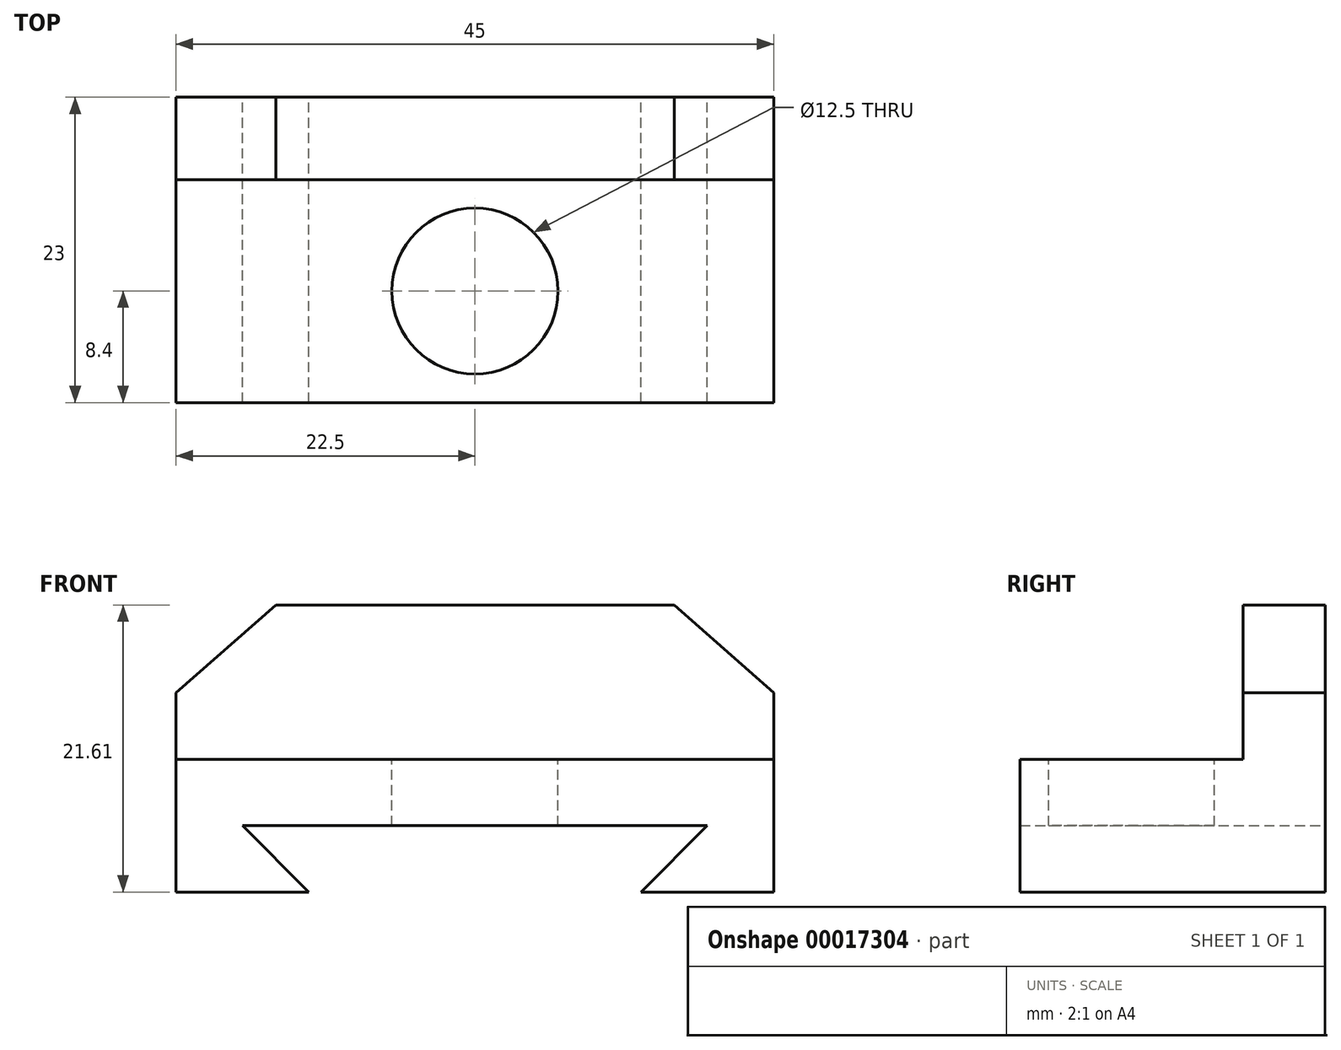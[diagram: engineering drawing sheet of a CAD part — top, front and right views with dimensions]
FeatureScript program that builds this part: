
annotation { "Feature Type Name" : "Feature", "Feature Type Description" : "" }
export const myFeature = defineFeature(function(context is Context, id is Id, definition is map)
    precondition{}
    {
        {
            var Q0;
            Q0=qCreatedBy(makeId("Front.planeOp"),FACE);
            var sketch = newSketch(context, id + "F0", { "sketchPlane" : qUnion([Q0])});
            skLineSegment(sketch, "E0", {"start": v(0, 15) * mm, "end": v(7.5, 21.61) * mm});
            skLineSegment(sketch, "E1", {"start": v(7.5, 21.61) * mm, "end": v(37.5, 21.61) * mm});
            skLineSegment(sketch, "E2", {"start": v(37.5, 21.61) * mm, "end": v(45, 15) * mm});
            skLineSegment(sketch, "E3", {"start": v(45, 15) * mm, "end": v(45, 0) * mm});
            skLineSegment(sketch, "E4", {"start": v(45, 10) * mm, "end": v(0, 10) * mm});
            skLineSegment(sketch, "E5", {"start": v(10, 0) * mm, "end": v(5, 5) * mm});
            skLineSegment(sketch, "E6", {"start": v(5, 5) * mm, "end": v(40, 5) * mm});
            skLineSegment(sketch, "E7", {"start": v(40, 5) * mm, "end": v(35, 0) * mm});
            skLineSegment(sketch, "E8", {"start": v(0, 0) * mm, "end": v(10, 0) * mm});
            skLineSegment(sketch, "E9", {"start": v(35, 0) * mm, "end": v(45, 0) * mm});
            skLineSegment(sketch, "E10", {"start": v(0, 5) * mm, "end": v(0, 0) * mm});
            skLineSegment(sketch, "E11", {"start": v(0, 15) * mm, "end": v(0, 5) * mm});
            skSolve(sketch);
        }
        {
            var Q0;
            {var subQ2=sQuery(id+"F0.wireOp",EDGE,"E4");Q0=makeQuery(id+"F0.imprint","IMPRINT",FACE,{"disambiguationData":[TD([[makeQuery(id+"F0.imprint","IMPRINT",EDGE,{"derivedFrom":subQ2}),1.0]])]});}
            var Q1;
            {var subQ2=sQuery(id+"F0.wireOp",EDGE,"E0");Q1=makeQuery(id+"F0.imprint","IMPRINT",FACE,{"disambiguationData":[TD([[makeQuery(id+"F0.imprint","IMPRINT",EDGE,{"derivedFrom":subQ2}),-1.0]])]});}
            extrude(context, id + "F1", {"entities" : qUnion([Q0, Q1]), "depth" : 6.2 * mm});
        }
        {
            var Q0;
            Q0=makeQuery(id+"F1.opExtrude","CAP_FACE",FACE,{"disambiguationData":[OSD([sQuery(id+"F0.wireOp",EDGE,"E0"),sQuery(id+"F0.wireOp",EDGE,"E1"),sQuery(id+"F0.wireOp",EDGE,"E2"),sQuery(id+"F0.wireOp",EDGE,"E3"),sQuery(id+"F0.wireOp",EDGE,"E5"),sQuery(id+"F0.wireOp",EDGE,"E6"),sQuery(id+"F0.wireOp",EDGE,"E7"),sQuery(id+"F0.wireOp",EDGE,"E8"),sQuery(id+"F0.wireOp",EDGE,"E9"),sQuery(id+"F0.wireOp",EDGE,"E10"),sQuery(id+"F0.wireOp",EDGE,"E11")])],"isStart":false});
            var sketch = newSketch(context, id + "F2", { "sketchPlane" : qUnion([Q0])});
            skLineSegment(sketch, "E12", {"start": v(0, 10) * mm, "end": v(45, 10) * mm});
            skLineSegment(sketch, "E13", {"start": v(0, 10) * mm, "end": v(0, 0) * mm});
            skSolve(sketch);
        }
        {
            var Q0;
            {var subQ1=sQuery(id+"F2.wireOp",EDGE,"E12");Q0=makeQuery(id+"F2.imprint","IMPRINT",FACE,{"disambiguationData":[TD([[makeQuery(id+"F2.imprint","IMPRINT",EDGE,{"derivedFrom":subQ1}),-1.0]])]});}
            extrude(context, id + "F3", {"entities" : qUnion([Q0]), "operationType" : NewBodyOperationType.ADD, "depth" : 16.8 * mm});
        }
        {
            var Q0;
            Q0=makeQuery(id+"F3.opExtrude","SWEPT_FACE",FACE,{"disambiguationData":[OSD([sQuery(id+"F2.wireOp",EDGE,"E12")])]});
            var sketch = newSketch(context, id + "F4", { "sketchPlane" : qUnion([Q0])});
            skCircle(sketch, "E14", {"center": v(22.5, -14.6) * mm, "radius": 6.25 * mm});
            skSolve(sketch);
        }
        {
            var Q0;
            Q0=makeQuery(id+"F4.imprint","IMPRINT",FACE,{"disambiguationData":[TD([[makeQuery(id+"F4.imprint","IMPRINT",EDGE,{"derivedFrom":sQuery(id+"F4.wireOp",EDGE,"E14")}),1.0]])]});
            extrude(context, id + "F5", {"entities" : qUnion([Q0]), "operationType" : NewBodyOperationType.REMOVE, "oppositeDirection" : true, "depth" : 25 * mm});
        }
    });
